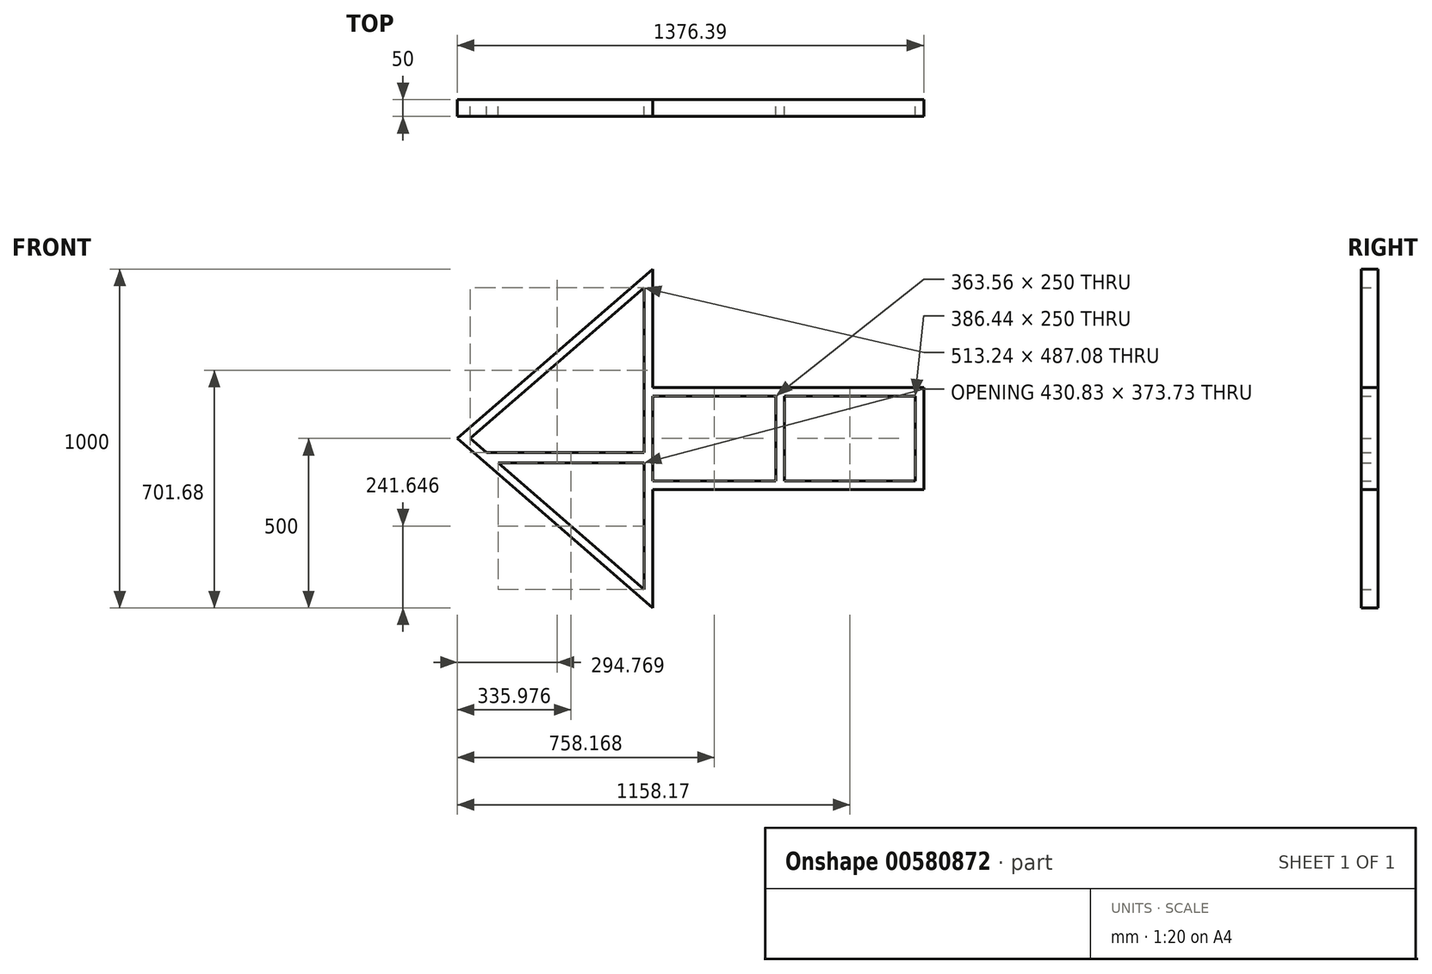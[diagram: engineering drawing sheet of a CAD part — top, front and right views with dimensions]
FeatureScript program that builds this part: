
annotation { "Feature Type Name" : "Feature", "Feature Type Description" : "" }
export const myFeature = defineFeature(function(context is Context, id is Id, definition is map)
    precondition{}
    {
        {
            var Q0;
            Q0=qCreatedBy(makeId("Front.planeOp"),FACE);
            var sketch = newSketch(context, id + "F0", { "sketchPlane" : qUnion([Q0])});
            skLineSegment(sketch, "E0", {"start": v(0, 500) * mm, "end": v(0, 150) * mm});
            skLineSegment(sketch, "E1", {"start": v(0, -500) * mm, "end": v(0, -150) * mm});
            skLineSegment(sketch, "E2", {"start": v(0, -500) * mm, "end": v(-576.4, 0) * mm});
            skLineSegment(sketch, "E3", {"start": v(0, 500) * mm, "end": v(-576.4, 0) * mm});
            skLineSegment(sketch, "E4", {"start": v(-25, -71.5) * mm, "end": v(-25, -420.5) * mm});
            skLineSegment(sketch, "E5", {"start": v(-284.56, -220.06) * mm, "end": v(-25, -445.22) * mm});
            skLineSegment(sketch, "E6", {"start": v(-284.56, -220.06) * mm, "end": v(-455.83, -71.5) * mm});
            skLineSegment(sketch, "E7", {"start": v(-25, -420.5) * mm, "end": v(-25, -445.22) * mm});
            skLineSegment(sketch, "E8", {"start": v(-455.83, -71.5) * mm, "end": v(-25, -71.5) * mm});
            skPoint(sketch, "E9.end.orphan", {"position": v(-490.68, -25) * mm});
            skPoint(sketch, "E9.start.orphan", {"position": v(-509.42, -25) * mm});
            skLineSegment(sketch, "E10", {"start": v(-25, -41.86) * mm, "end": v(-455.83, -41.86) * mm});
            skLineSegment(sketch, "E11", {"start": v(-489.99, -41.86) * mm, "end": v(-455.83, -41.86) * mm});
            skLineSegment(sketch, "E12", {"start": v(-489.99, -41.86) * mm, "end": v(-538.24, 0) * mm});
            skLineSegment(sketch, "E13", {"start": v(-538.24, 0) * mm, "end": v(-25, 445.22) * mm});
            skLineSegment(sketch, "E14", {"start": v(-25, -41.86) * mm, "end": v(-25, 445.22) * mm});
            skLineSegment(sketch, "E15.bottom", {"start": v(0, 150) * mm, "end": v(800, 150) * mm});
            skLineSegment(sketch, "E15.top", {"start": v(0, -150) * mm, "end": v(800, -150) * mm});
            skLineSegment(sketch, "E15.right", {"start": v(800, 150) * mm, "end": v(800, -150) * mm});
            skLineSegment(sketch, "E16.bottom", {"start": v(0, 125) * mm, "end": v(363.56, 125) * mm});
            skLineSegment(sketch, "E16.top", {"start": v(0, -125) * mm, "end": v(363.56, -125) * mm});
            skLineSegment(sketch, "E16.left", {"start": v(0, 125) * mm, "end": v(0, -125) * mm});
            skLineSegment(sketch, "E16.right", {"start": v(363.56, 125) * mm, "end": v(363.56, -125) * mm});
            skLineSegment(sketch, "E17.bottom", {"start": v(388.56, 125) * mm, "end": v(775, 125) * mm});
            skLineSegment(sketch, "E17.top", {"start": v(388.56, -125) * mm, "end": v(775, -125) * mm});
            skLineSegment(sketch, "E17.left", {"start": v(388.56, 125) * mm, "end": v(388.56, -125) * mm});
            skLineSegment(sketch, "E17.right", {"start": v(775, 125) * mm, "end": v(775, -125) * mm});
            skLineSegment(sketch, "E18.trimOffspring", {"start": v(0, -150) * mm, "end": v(0, -500) * mm});
            skPoint(sketch, "E15.left.start.orphan", {"position": v(0, 0) * mm});
            skSolve(sketch);
        }
        {
            var Q0;
            Q0 = qSketchRegion(id + "F0", true);
            extrude(context, id + "F1", {"entities" : qUnion([Q0]), "depth" : 50 * mm, "offsetDistance" : 25 * mm});
        }
    });
